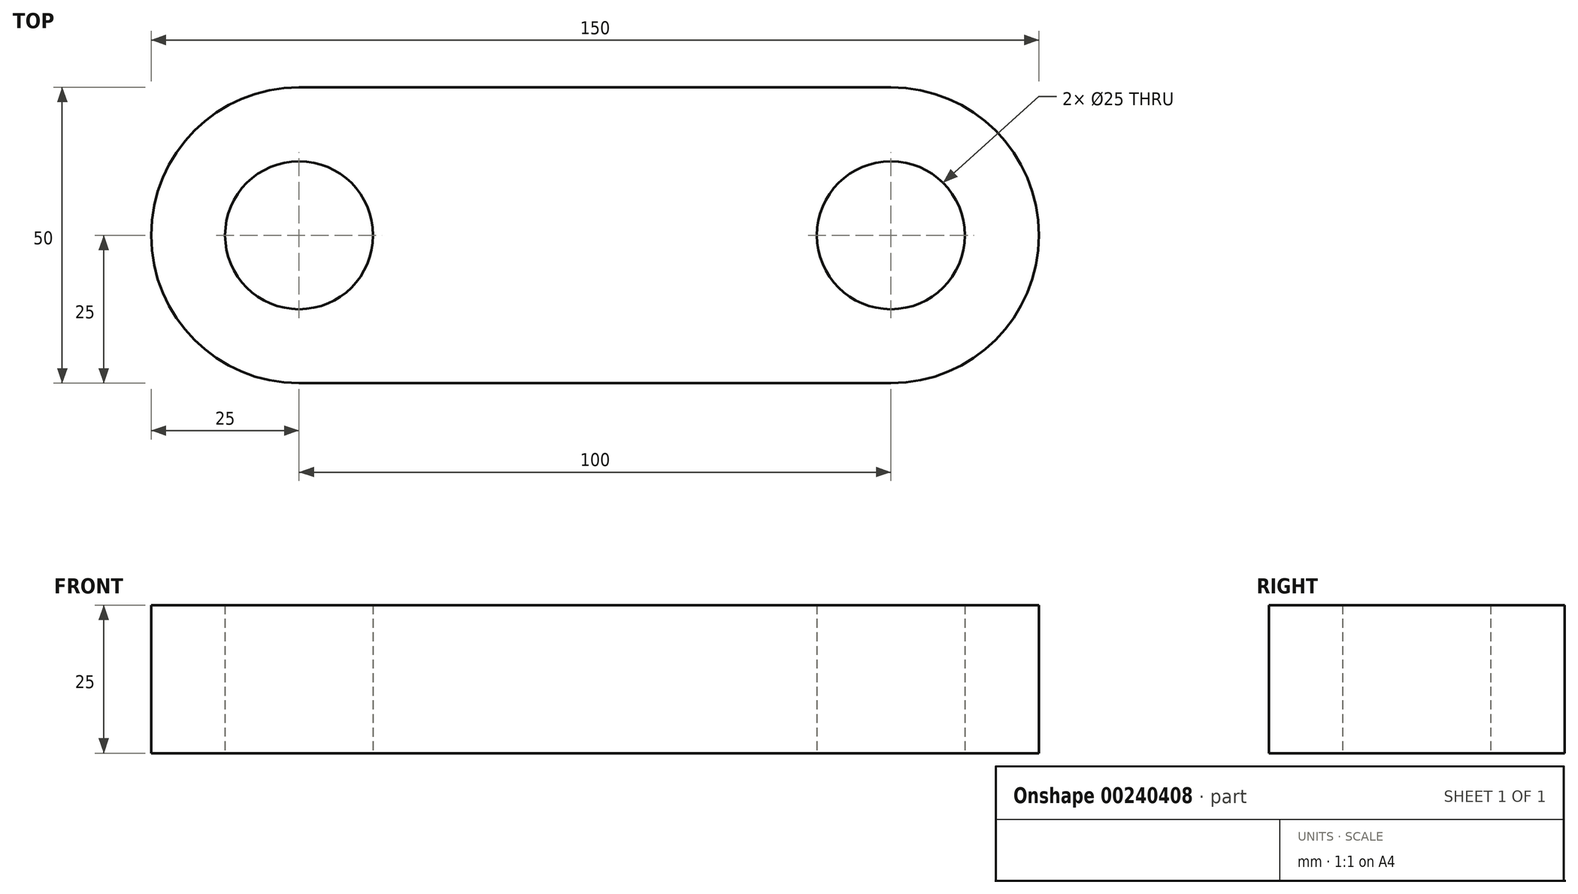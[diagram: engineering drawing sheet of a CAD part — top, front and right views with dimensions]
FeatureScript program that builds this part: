
annotation { "Feature Type Name" : "Feature", "Feature Type Description" : "" }
export const myFeature = defineFeature(function(context is Context, id is Id, definition is map)
    precondition{}
    {
        {
            var Q0;
            Q0=qCreatedBy(makeId("Top.planeOp"),FACE);
            var sketch = newSketch(context, id + "F0", { "sketchPlane" : qUnion([Q0])});
            skLineSegment(sketch, "E0.rect.bottom", {"start": v(50, 25) * mm, "end": v(-50, 25) * mm});
            skLineSegment(sketch, "E0.rect.top", {"start": v(50, -25) * mm, "end": v(-50, -25) * mm});
            skPoint(sketch, "E0.rect.middle", {"position": v(0, 0) * mm});
            skArc(sketch, "E1", {"start": v(-50, 25) * mm, "mid": v(-75, 0) * mm, "end": v(-50, -25) * mm});
            skArc(sketch, "E2", {"start": v(50, -25) * mm, "mid": v(75, 0) * mm, "end": v(50, 25) * mm});
            skCircle(sketch, "E3", {"center": v(-50, 0) * mm, "radius": 12.5 * mm});
            skCircle(sketch, "E4", {"center": v(50, 0) * mm, "radius": 12.5 * mm});
            skSolve(sketch);
        }
        {
            var Q0;
            Q0=qSketchRegion(id+"F0",true);
            extrude(context, id + "F1", {"entities" : qUnion([Q0]), "depth" : 25 * mm});
        }
    });
